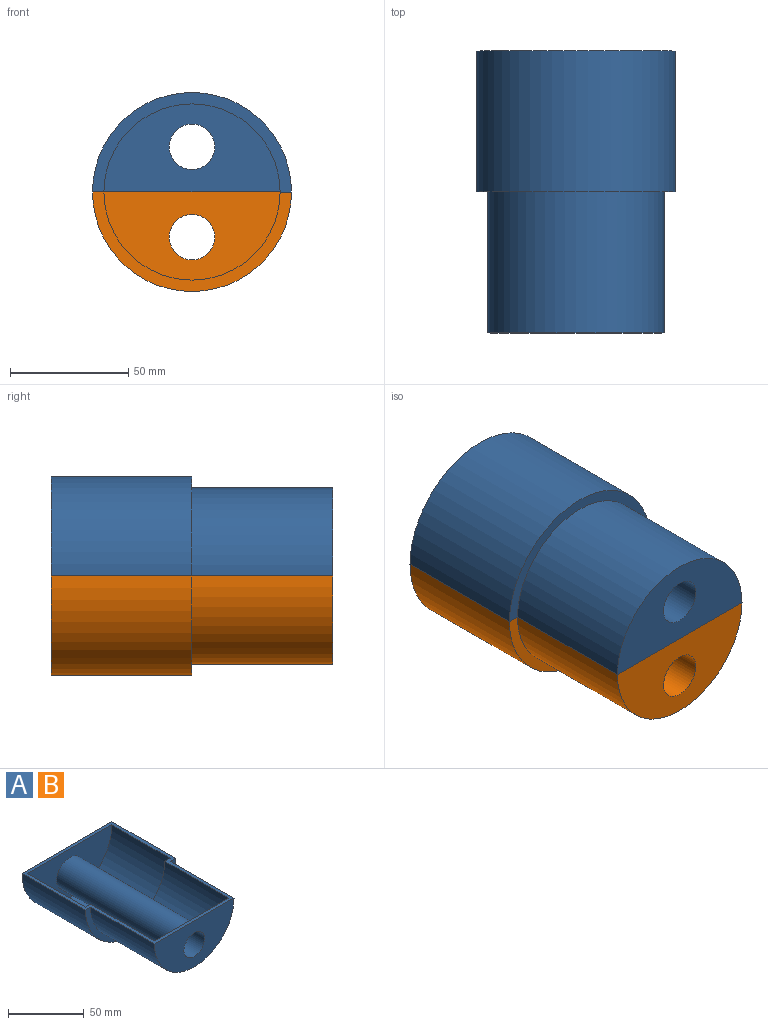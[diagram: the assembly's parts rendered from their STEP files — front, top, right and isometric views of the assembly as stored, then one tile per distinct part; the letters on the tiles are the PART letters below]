
ASSEMBLY  parts=2 mates=1
PART A: 13 faces, bbox 84x119x42 mm
  f0: plane 119x83.99mm, normal (0,0,1), area 990mm2, adj f1,f2,f3,f4,f5,f7,f8,f9
  f1: cylinder r=42mm len=83.99mm, axis (0,-1,0), area 7836.9mm2, adj f0,f2,f3
  f2: plane 83.99x42mm, normal (0,1,0), area 2480.8mm2, adj f0,f1,f6
  f3: plane 83.99x42mm, normal (0,-1,0), area 598.7mm2, adj f0,f1,f4
  f4: cylinder r=37.18mm len=74.37mm, axis (0,1,0), area 6962mm2, adj f0,f3,f5
  f5: plane 74.37x37.18mm, normal (0,-1,0), area 1882.1mm2, adj f0,f4,f6
  f6: cylinder r=9.6mm len=119mm, axis (0,-1,0), area 7178.4mm2, adj f2,f5
  f7: cylinder r=39.5mm len=78.99mm, axis (0,-1,0), area 6750mm2, adj f0,f8,f9
  f8: plane 78.99x39.5mm, normal (0,-1,0), area 1990.3mm2, adj f0,f7,f12
  f9: plane 78.99x39.5mm, normal (0,1,0), area 560.9mm2, adj f0,f7,f10
  f10: cylinder r=34.68mm len=69.37mm, axis (0,1,0), area 6493.9mm2, adj f0,f9,f11
  f11: plane 69.37x34.68mm, normal (0,1,0), area 1429.5mm2, adj f0,f10,f12
  f12: cylinder r=12.1mm len=114mm, axis (0,-1,0), area 8667.5mm2, adj f8,f11
PART B: same geometry as A
PLACE A rot(axis=(0,-1,0),180deg) t=(7.9,21.94,-6.34)mm
PLACE B rot(axis=(-0.17,0.16,0.97),0deg) t=(7.9,21.94,-6.34)mm
MATE fastened A.f0 <-> B.f0  axis (0,0,-1) through (45.09,-37.66,-6.34)mm
